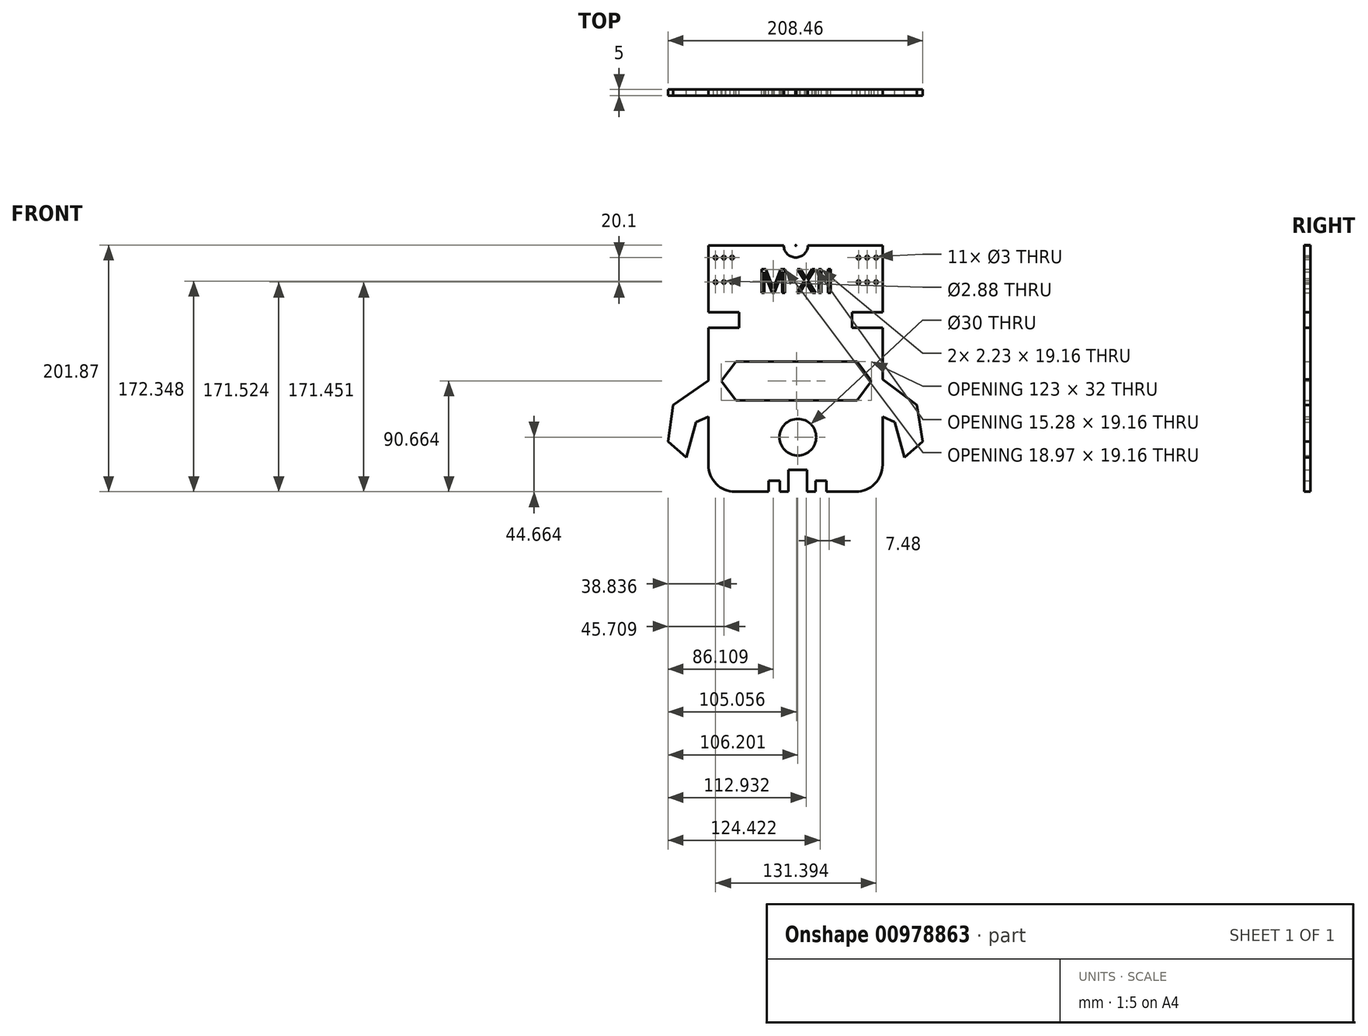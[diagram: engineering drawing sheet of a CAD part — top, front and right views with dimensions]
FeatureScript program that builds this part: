
annotation { "Feature Type Name" : "Feature", "Feature Type Description" : "" }
export const myFeature = defineFeature(function(context is Context, id is Id, definition is map)
    precondition{}
    {
        {
            var Q0;
            Q0=qCreatedBy(makeId("Front.planeOp"),FACE);
            var sketch = newSketch(context, id + "F0", { "sketchPlane" : qUnion([Q0])});
            skLineSegment(sketch, "E0.bottom", {"start": v(-119.04, 78.42) * mm, "end": v(-57.4, 78.42) * mm});
            skLineSegment(sketch, "E0.top", {"start": v(-97.04, -123.13) * mm, "end": v(-69.7, -123.13) * mm});
            skLineSegment(sketch, "E0.left", {"start": v(-119.04, 78.42) * mm, "end": v(-119.04, 23.58) * mm});
            skLineSegment(sketch, "E0.right", {"start": v(23.44, 78.42) * mm, "end": v(23.44, 23.58) * mm});
            skLineSegment(sketch, "E1", {"start": v(-47.5, 102.75) * mm, "end": v(-47.5, 78.1) * mm});
            skLineSegment(sketch, "E2.left", {"start": v(23.44, 78.42) * mm, "end": v(23.44, 68.42) * mm});
            skText(sketch, "E3", { "text": "M XII", "fontName": "OpenSans-Regular.ttf"});
            skLineSegment(sketch, "E4.bottom", {"start": v(-96.47, -16.47) * mm, "end": v(2.53, -16.47) * mm});
            skLineSegment(sketch, "E4.top", {"start": v(-96.47, -48.47) * mm, "end": v(2.53, -48.47) * mm});
            skCircle(sketch, "E5", {"center": v(-45.83, -78.47) * mm, "radius": 15 * mm});
            skLineSegment(sketch, "E6", {"start": v(-96.47, -16.47) * mm, "end": v(-108.47, -32.47) * mm});
            skLineSegment(sketch, "E7", {"start": v(-108.47, -32.47) * mm, "end": v(-96.47, -48.47) * mm});
            skLineSegment(sketch, "E8", {"start": v(2.53, -16.47) * mm, "end": v(14.53, -32.47) * mm});
            skLineSegment(sketch, "E9", {"start": v(14.53, -32.47) * mm, "end": v(2.53, -48.47) * mm});
            skCircle(sketch, "E10", {"center": v(-47.5, 78.42) * mm, "radius": 0.32 * mm});
            skCircle(sketch, "E11", {"center": v(-113.2, 68.35) * mm, "radius": 1.5 * mm});
            skCircle(sketch, "E12", {"center": v(-113.2, 48.32) * mm, "radius": 1.5 * mm});
            skCircle(sketch, "E13", {"center": v(-99.6, 68.42) * mm, "radius": 1.5 * mm});
            skCircle(sketch, "E14", {"center": v(-106.32, 68.4) * mm, "radius": 1.5 * mm});
            skCircle(sketch, "E15", {"center": v(-106.32, 48.4) * mm, "radius": 1.44 * mm});
            skCircle(sketch, "E16", {"center": v(-99.6, 48.33) * mm, "radius": 1.5 * mm});
            skCircle(sketch, "E17", {"center": v(10.93, 68.42) * mm, "radius": 1.5 * mm});
            skCircle(sketch, "E18", {"center": v(3.81, 68.42) * mm, "radius": 1.5 * mm});
            skCircle(sketch, "E19", {"center": v(18.2, 48.33) * mm, "radius": 1.5 * mm});
            skCircle(sketch, "E20", {"center": v(18.2, 68.42) * mm, "radius": 1.5 * mm});
            skCircle(sketch, "E21", {"center": v(3.81, 48.33) * mm, "radius": 1.5 * mm});
            skCircle(sketch, "E22", {"center": v(10.93, 48.33) * mm, "radius": 1.5 * mm});
            skArc(sketch, "E23.filletArc", {"start": v(-119.04, -101.13) * mm, "mid": v(-112.6, -116.68) * mm, "end": v(-97.04, -123.13) * mm});
            skArc(sketch, "E24.filletArc", {"start": v(1.44, -123.13) * mm, "mid": v(17, -116.68) * mm, "end": v(23.44, -101.13) * mm});
            skLineSegment(sketch, "E25.top", {"start": v(-53.7, -105.13) * mm, "end": v(-38.44, -105.13) * mm});
            skLineSegment(sketch, "E25.left", {"start": v(-53.7, -123.13) * mm, "end": v(-53.7, -105.13) * mm});
            skLineSegment(sketch, "E25.right", {"start": v(-38.44, -123.13) * mm, "end": v(-38.44, -105.13) * mm});
            skLineSegment(sketch, "E26.trimOffspring", {"start": v(-38.44, -123.13) * mm, "end": v(-31.44, -123.13) * mm});
            skLineSegment(sketch, "E27.bottom", {"start": v(-119.04, 23.58) * mm, "end": v(-94.04, 23.58) * mm});
            skLineSegment(sketch, "E27.top", {"start": v(-119.04, 11.08) * mm, "end": v(-94.04, 11.08) * mm});
            skLineSegment(sketch, "E27.right", {"start": v(-94.04, 23.58) * mm, "end": v(-94.04, 11.08) * mm});
            skLineSegment(sketch, "E28.bottom", {"start": v(23.44, 23.58) * mm, "end": v(-1.56, 23.58) * mm});
            skLineSegment(sketch, "E28.top", {"start": v(23.44, 11.08) * mm, "end": v(-1.56, 11.08) * mm});
            skLineSegment(sketch, "E28.right", {"start": v(-1.56, 23.58) * mm, "end": v(-1.56, 11.08) * mm});
            skLineSegment(sketch, "E29.trimOffspring", {"start": v(23.44, 11.08) * mm, "end": v(23.44, -101.13) * mm});
            skLineSegment(sketch, "E30.trimOffspring", {"start": v(-119.04, 11.08) * mm, "end": v(-119.04, -101.13) * mm});
            skArc(sketch, "E31", {"start": v(-57.4, 78.42) * mm, "mid": v(-47.5, 68.53) * mm, "end": v(-37.62, 78.42) * mm});
            skLineSegment(sketch, "E32.trimOffspring", {"start": v(-47.83, 78.42) * mm, "end": v(-47.18, 78.42) * mm});
            skLineSegment(sketch, "E33.trimOffspring", {"start": v(-37.62, 78.42) * mm, "end": v(23.44, 78.42) * mm});
            skLineSegment(sketch, "E34.trimOffspring", {"start": v(-47.5, 68.53) * mm, "end": v(-47.5, -10.48) * mm});
            skLineSegment(sketch, "E35", {"start": v(-119.04, -32.15) * mm, "end": v(-147.75, -52.17) * mm});
            skLineSegment(sketch, "E36", {"start": v(23.44, -31.28) * mm, "end": v(51.44, -52.28) * mm});
            skLineSegment(sketch, "E37", {"start": v(-147.75, -52.17) * mm, "end": v(-152.03, -81.86) * mm});
            skLineSegment(sketch, "E38", {"start": v(51.44, -52.28) * mm, "end": v(56.43, -81.86) * mm});
            skLineSegment(sketch, "E39", {"start": v(-152.03, -81.86) * mm, "end": v(-137.05, -95.11) * mm});
            skLineSegment(sketch, "E40", {"start": v(56.43, -81.86) * mm, "end": v(41.45, -95.11) * mm});
            skLineSegment(sketch, "E41", {"start": v(-137.05, -95.11) * mm, "end": v(-129.04, -66.2) * mm});
            skLineSegment(sketch, "E42", {"start": v(41.45, -95.11) * mm, "end": v(33.44, -66.2) * mm});
            skLineSegment(sketch, "E43", {"start": v(-129.04, -66.2) * mm, "end": v(-119.04, -61.6) * mm});
            skLineSegment(sketch, "E44", {"start": v(33.44, -66.2) * mm, "end": v(23.44, -61.6) * mm});
            skLineSegment(sketch, "E45.top", {"start": v(-69.7, -114.13) * mm, "end": v(-60.7, -114.13) * mm});
            skLineSegment(sketch, "E45.left", {"start": v(-69.7, -123.13) * mm, "end": v(-69.7, -114.13) * mm});
            skLineSegment(sketch, "E45.right", {"start": v(-60.7, -123.13) * mm, "end": v(-60.7, -114.13) * mm});
            skLineSegment(sketch, "E46.bottom", {"start": v(-31.44, -114.13) * mm, "end": v(-22.44, -114.13) * mm});
            skLineSegment(sketch, "E46.left", {"start": v(-31.44, -114.13) * mm, "end": v(-31.44, -123.13) * mm});
            skLineSegment(sketch, "E46.right", {"start": v(-22.44, -114.13) * mm, "end": v(-22.44, -123.13) * mm});
            skLineSegment(sketch, "E47.trimOffspring", {"start": v(-22.44, -123.13) * mm, "end": v(1.44, -123.13) * mm});
            skLineSegment(sketch, "E48.trimOffspring", {"start": v(-60.7, -123.13) * mm, "end": v(-53.7, -123.13) * mm});
            const initialGuessF0  = {"E3": [-0.07804, 0.03964, 1, 0, 0.01932]};
            skSetInitialGuess(sketch, initialGuessF0);
            skSolve(sketch);
        }
        {
            var Q0;
            {var subQ0=sQuery(id+"F0.wireOp",EDGE,"E0.bottom");Q0=makeQuery(id+"F0.imprint","IMPRINT",FACE,{"disambiguationData":[TD([[makeQuery(id+"F0.imprint","IMPRINT",EDGE,{"derivedFrom":subQ0}),-1.0]])]});}
            var Q1;
            {var subQ0=sQuery(id+"F0.wireOp",EDGE,"E35");Q1=makeQuery(id+"F0.imprint","IMPRINT",FACE,{"disambiguationData":[TD([[makeQuery(id+"F0.imprint","IMPRINT",EDGE,{"derivedFrom":subQ0}),1.0]])]});}
            var Q2;
            {var subQ0=sQuery(id+"F0.wireOp",EDGE,"E36");Q2=makeQuery(id+"F0.imprint","IMPRINT",FACE,{"disambiguationData":[TD([[makeQuery(id+"F0.imprint","IMPRINT",EDGE,{"derivedFrom":subQ0}),-1.0]])]});}
            extrude(context, id + "F1", {"entities" : qUnion([Q0, Q1, Q2]), "depth" : 5 * mm, "offsetDistance" : 25 * mm});
        }
        {
            var Q0;
            Q0 = qSketchRegion(id + "F0", true);
            extrude(context, id + "F2", {"entities" : qUnion([Q0]), "operationType" : NewBodyOperationType.ADD, "depth" : 5 * mm, "offsetDistance" : 25 * mm});
        }
    });
